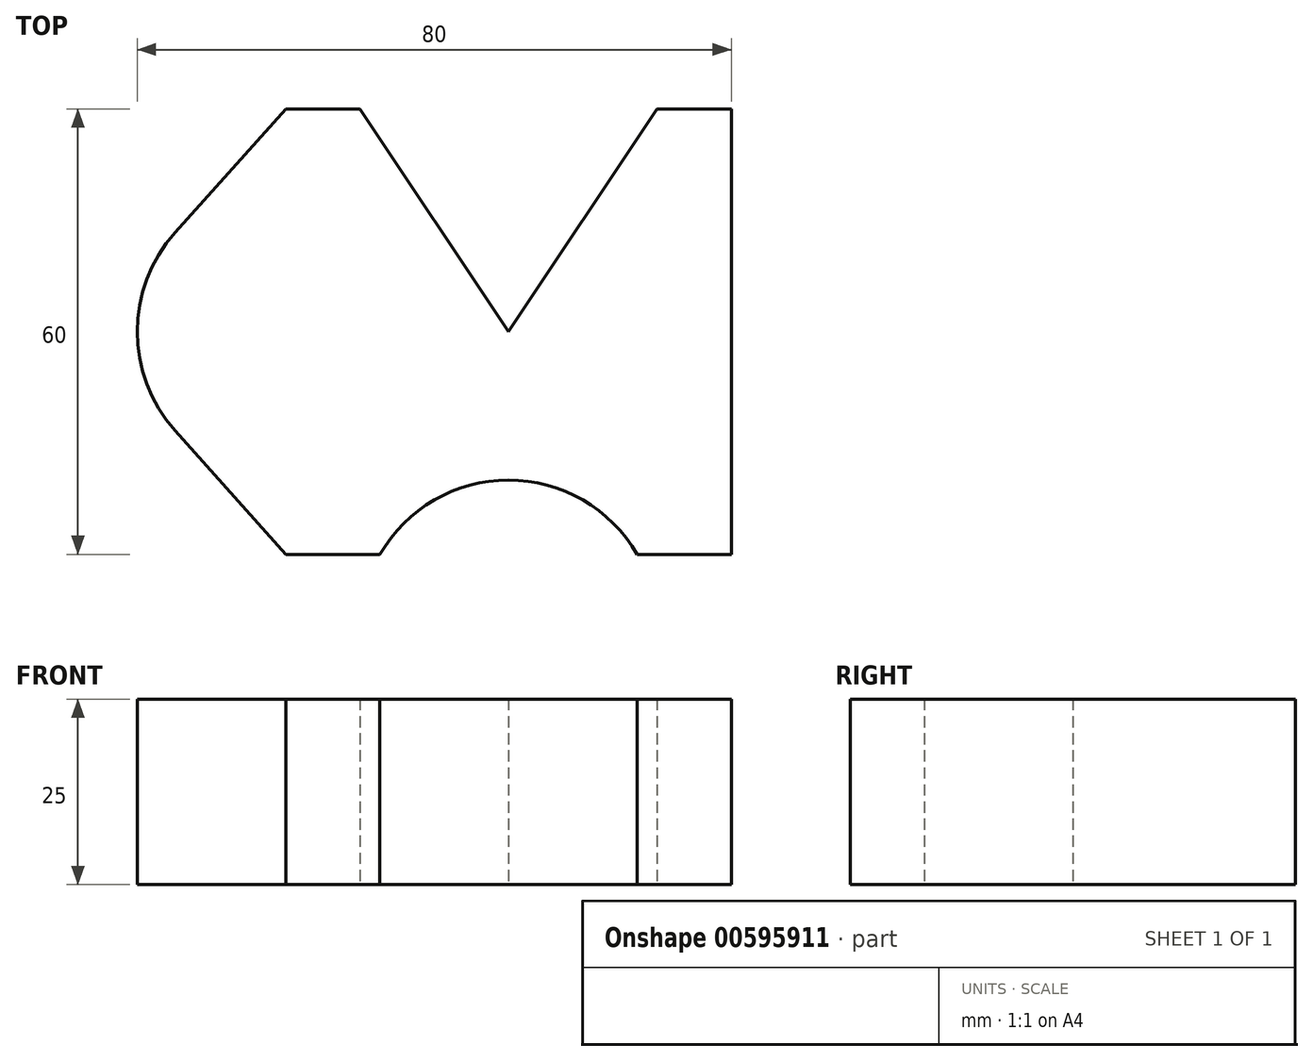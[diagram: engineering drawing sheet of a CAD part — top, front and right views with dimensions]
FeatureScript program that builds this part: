
annotation { "Feature Type Name" : "Feature", "Feature Type Description" : "" }
export const myFeature = defineFeature(function(context is Context, id is Id, definition is map)
    precondition{}
    {
        {
            var Q0;
            Q0=qCreatedBy(makeId("Top.planeOp"),FACE);
            var sketch = newSketch(context, id + "F0", { "sketchPlane" : qUnion([Q0])});
            skLineSegment(sketch, "E0", {"start": v(30, 30) * mm, "end": v(30, -30) * mm});
            skLineSegment(sketch, "E1", {"start": v(30, -30) * mm, "end": v(17.32, -30) * mm});
            skArc(sketch, "E2", {"start": v(17.32, -30) * mm, "mid": v(0, -20) * mm, "end": v(-17.32, -30) * mm});
            skLineSegment(sketch, "E3", {"start": v(-17.32, -30) * mm, "end": v(-30, -30) * mm});
            skLineSegment(sketch, "E4", {"start": v(-30, -30) * mm, "end": v(-44.9, -13.33) * mm});
            skArc(sketch, "E5", {"start": v(-44.9, 13.33) * mm, "mid": v(-50, 0) * mm, "end": v(-44.9, -13.33) * mm});
            skLineSegment(sketch, "E6", {"start": v(-44.9, 13.33) * mm, "end": v(-30, 30) * mm});
            skLineSegment(sketch, "E7", {"start": v(-30, 30) * mm, "end": v(-20, 30) * mm});
            skLineSegment(sketch, "E8", {"start": v(-20, 30) * mm, "end": v(0, 0) * mm});
            skLineSegment(sketch, "E9", {"start": v(0, 0) * mm, "end": v(20, 30) * mm});
            skLineSegment(sketch, "E10", {"start": v(20, 30) * mm, "end": v(30, 30) * mm});
            skLineSegment(sketch, "E11", {"start": v(-30, 30) * mm, "end": v(-30, -30) * mm, "construction": true});
            skSolve(sketch);
        }
        {
            var Q0;
            Q0=makeQuery(id+"F0.imprint","IMPRINT",FACE,{"disambiguationData":[TD([[makeQuery(id+"F0.imprint","IMPRINT",EDGE,{"derivedFrom":sQuery(id+"F0.wireOp",EDGE,"E0")}),-1.0]])]});
            extrude(context, id + "F1", {"entities" : qUnion([Q0]), "depth" : 25 * mm, "offsetDistance" : 25 * mm});
        }
    });
